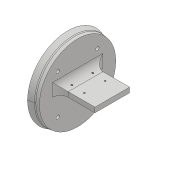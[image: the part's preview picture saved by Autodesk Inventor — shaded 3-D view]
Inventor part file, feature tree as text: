
AUTODESK INVENTOR PART (.ipt)
format: ipt  version: 2018 (Build 220112000, 112)  size: 468,992 bytes
history: native  units: mm
features: sketch x13, fillet x9, extrude x8, projected_geometry x5, hole x3, revolve x2, plane x2, shell x1, pattern_circular x1
ambient origin geometry x8: Origin, YZ Plane, XZ Plane, XY Plane, X Axis, Y Axis, Z Axis, Center Point
bodies: Solid1 (feature_tree), Solid3 (feature_tree)
feature tree (44):
  revolve  "Revolution1"  [1 undecoded]
  fillet  "Fillet1"  Radius=45.0mm
  shell  "Shell1"  Thickness=45.0mm
  fillet  "Fillet3"  Radius=10.0mm
  plane  "Work Plane1"
  extrude  "Extrusion1"  Depth=22.0mm
  hole  "Hole1"  [1 undecoded]
  extrude  "Extrusion3"  Depth=25.0mm
  fillet  "Fillet4"  Radius=1.0mm
  pattern_circular  "Circular Pattern1"  Count=5  [1 undecoded]
  extrude  "Extrusion4"  Depth=10.0mm
  fillet  "Fillet5"  Radius=10.0mm
  fillet  "Fillet6"  Radius=8.0mm
  fillet  "Fillet7"  Radius=30.0mm
  fillet  "Fillet8"  Radius=8.0mm
  plane  "Work Plane2"
  extrude  "Extrusion5"  TaperAngle=0.0deg  [1 undecoded]
  extrude  "Extrusion6"  Depth=60.0mm TaperAngle=360.0deg
  revolve  "Revolution2"  [1 undecoded]
  extrude  "Extrusion7"  Depth=8.0mm
  hole  "Hole2"  [1 undecoded]
  extrude  "Extrusion8"  Depth=10.0mm TaperAngle=0.0deg
  fillet  "Fillet9"  [1 undecoded]
  extrude  "Extrusion9"  TaperAngle=90.0deg  [1 undecoded]
  fillet  "Fillet10"  [1 undecoded]
  hole  "Hole3"  [1 undecoded]
  sketch  "Sketch1"  dims[d0=125.0mm d1=40.0mm d2=45.0mm d3=45.0mm d4=10.0mm]
  sketch  "Sketch2"  dims[d5=70.0mm d6=22.0mm]
  sketch  "Sketch4"  dims[d7=70.0mm d8=90.0deg]
  projected_geometry  "Projected Loop2"
  sketch  "Sketch5"  dims[d9=17.104227mm d10=25.0mm d12=1.0mm]
  sketch  "Sketch6"  dims[d13=0.25mm d14=50.0mm]
  projected_geometry  "Projected Loop3"
  sketch  "Sketch7"  dims[d15=15.0mm d16=38.0mm d17=10.0mm d18=0.0mm d22=8.0mm]
  sketch  "Sketch10"  dims[d23=3.2mm d24=6.0mm d25=6.3mm d26=2.0mm d27=90.0deg d28=15.0mm d29=20.594885mm d30=30.0mm d31=8.0mm]
  sketch  "Sketch11"  dims[d32=40.0mm d33=0.0mm d34=0.0mm]
  projected_geometry  "Projected Loop4"
  sketch  "Sketch12"  dims[d35=2.0mm d36=60.0mm d37=360.0deg]
  sketch  "Sketch13"  dims[d39=20.0mm d40=10.0mm d41=0.0mm]
  sketch  "Sketch14"  dims[d42=8.0mm d43=8.0mm]
  sketch  "Sketch15"  dims[d44=3.0mm d45=3.5mm]
  projected_geometry  "Projected Loop5"
  sketch  "Sketch16"  dims[d46=50.0mm d47=10.0mm d48=0.0mm d49=0.0mm d50=0.0mm d51=90.0deg d52=0.0mm d53=0.0mm d54=40.0mm d55=40.0mm d56=3.4mm d57=10.0mm d58=4.0mm d59=2.0mm d60=90.0deg d61=8.0mm d62=20.594885mm d63=5.0mm d64=25.0mm d65=10.0mm d66=0.0mm d67=2.0mm d68=5.0mm d69=35.0mm d70=35.0mm d71=0.0mm d72=8.0mm d73=12.5mm d74=21.0mm d75=24.0mm d76=1.567mm d77=10.0mm d78=4.0mm d79=2.0mm d80=90.0deg d81=6.3mm d82=20.594885mm]
  projected_geometry  "Project Cut Edges1"
note: 10 required parameter values undecoded (feature->parameter linkage not recoverable at this tier; creation-order binding heuristic only, values carry confidence <= 0.55)